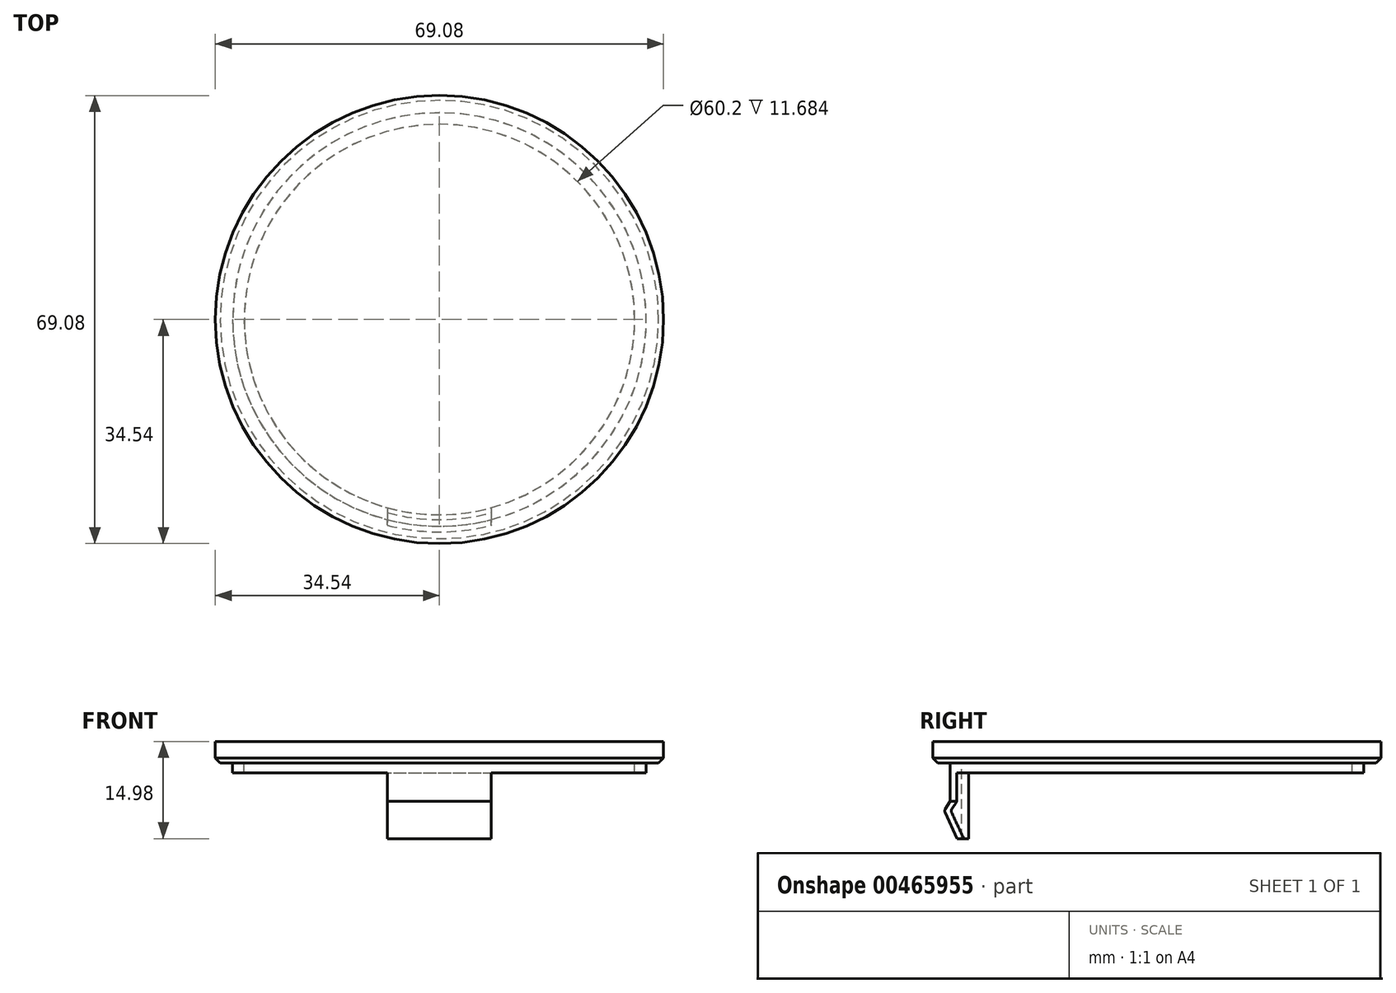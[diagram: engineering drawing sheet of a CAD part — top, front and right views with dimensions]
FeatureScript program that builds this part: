
annotation { "Feature Type Name" : "Feature", "Feature Type Description" : "" }
export const myFeature = defineFeature(function(context is Context, id is Id, definition is map)
    precondition{}
    {
        {
            var Q0;
            Q0=qCreatedBy(makeId("Top.planeOp"),FACE);
            var sketch = newSketch(context, id + "F0", { "sketchPlane" : qUnion([Q0])});
            skCircle(sketch, "E0", {"center": v(0, 0) * mm, "radius": 34.54 * mm});
            skSolve(sketch);
        }
        {
            var Q0;
            Q0=makeQuery(id+"F0.imprint","IMPRINT",FACE,{"disambiguationData":[TD([[makeQuery(id+"F0.imprint","IMPRINT",EDGE,{"derivedFrom":sQuery(id+"F0.wireOp",EDGE,"E0")}),1.0]])]});
            extrude(context, id + "F1", {"entities" : qUnion([Q0]), "depth" : 3.3 * mm});
        }
        {
            var Q0;
            Q0=makeQuery(id+"F1.opExtrude","CAP_FACE",FACE,{"disambiguationData":[OSD([sQuery(id+"F0.wireOp",EDGE,"E0")])],"isStart":true});
            var sketch = newSketch(context, id + "F2", { "sketchPlane" : qUnion([Q0])});
            skCircle(sketch, "E1", {"center": v(0, 0) * mm, "radius": 31.88 * mm});
            skCircle(sketch, "E2", {"center": v(0, 0) * mm, "radius": 30.1 * mm});
            skSolve(sketch);
        }
        {
            var Q0;
            Q0 = qSketchRegion(id + "F2", true);
            extrude(context, id + "F3", {"entities" : qUnion([Q0]), "operationType" : NewBodyOperationType.ADD, "depth" : 1.52 * mm});
        }
        {
            var Q0;
            Q0=qCreatedBy(makeId("Right.planeOp"),FACE);
            var sketch = newSketch(context, id + "F4", { "sketchPlane" : qUnion([Q0])});
            skLineSegment(sketch, "E3", {"start": v(0, 0) * mm, "end": v(0, -19.85) * mm});
            skSolve(sketch);
        }
        {
            var Q0;
            Q0=makeQuery(id+"F3.opExtrude","CAP_FACE",FACE,{"disambiguationData":[OSD([sQuery(id+"F2.wireOp",EDGE,"E1"),sQuery(id+"F2.wireOp",EDGE,"E2")])],"isStart":false});
            var sketch = newSketch(context, id + "F5", { "sketchPlane" : qUnion([Q0])});
            skArc(sketch, "E4", {"start": v(8, 29.02) * mm, "mid": v(0, 30.1) * mm, "end": v(-8, 29.02) * mm});
            skLineSegment(sketch, "E5", {"start": v(-8, 29.02) * mm, "end": v(-8, 31.81) * mm});
            skLineSegment(sketch, "E6", {"start": v(8, 29.02) * mm, "end": v(8, 31.81) * mm});
            skArc(sketch, "E7", {"start": v(8, 31.81) * mm, "mid": v(0, 32.8) * mm, "end": v(-8, 31.81) * mm});
            skSolve(sketch);
        }
        {
            var Q0;
            Q0 = qSketchRegion(id + "F5", true);
            extrude(context, id + "F6", {"entities" : qUnion([Q0]), "operationType" : NewBodyOperationType.ADD, "depth" : 10.16 * mm});
        }
        {
            var Q0;
            Q0=qCreatedBy(makeId("Right.planeOp"),FACE);
            var sketch = newSketch(context, id + "F7", { "sketchPlane" : qUnion([Q0])});
            skLineSegment(sketch, "E8", {"start": v(-31.88, -0.11) * mm, "end": v(-31.88, -5.95) * mm});
            skLineSegment(sketch, "E9", {"start": v(-30.08, -11.68) * mm, "end": v(-30.84, -11.68) * mm});
            skLineSegment(sketch, "E10", {"start": v(-30.08, -11.68) * mm, "end": v(-30.08, -13.13) * mm});
            skLineSegment(sketch, "E11", {"start": v(-30.08, -13.13) * mm, "end": v(-34.6, -13.13) * mm});
            skLineSegment(sketch, "E12", {"start": v(-34.6, -13.13) * mm, "end": v(-34.6, -0.11) * mm});
            skLineSegment(sketch, "E13", {"start": v(-34.6, -0.11) * mm, "end": v(-31.88, -0.11) * mm});
            skPoint(sketch, "E14", {"position": v(-32.8, -7.37) * mm});
            skLineSegment(sketch, "E15", {"start": v(-30.84, -11.68) * mm, "end": v(-32.69, -7.62) * mm});
            skLineSegment(sketch, "E16", {"start": v(-32.65, -7.13) * mm, "end": v(-31.88, -5.95) * mm});
            skArc(sketch, "E17.filletArc", {"start": v(-32.65, -7.13) * mm, "mid": v(-32.73, -7.37) * mm, "end": v(-32.69, -7.62) * mm});
            skSolve(sketch);
        }
        {
            var Q0;
            Q0 = qSketchRegion(id + "F7", true);
            var Q1;
            Q1=sQuery(id+"F4.wireOp",EDGE,"E3");
            revolve(context, id + "F8", {"operationType" : NewBodyOperationType.REMOVE, "entities" : qUnion([Q0]), "axis" : qUnion([Q1]), "revolveType" : RevolveType.FULL, "oppositeDirection" : true});
        }
        {
            var Q0;
            Q0=makeQuery(id+"F1.opExtrude","CAP_EDGE",EDGE,{"disambiguationData":[OSD([sQuery(id+"F0.wireOp",EDGE,"E0")])],"isStart":true});
            chamfer(context, id + "F9", {"entities" : qUnion([Q0]), "width" : 0.76 * mm, "tangentPropagation" : true});
        }
    });
